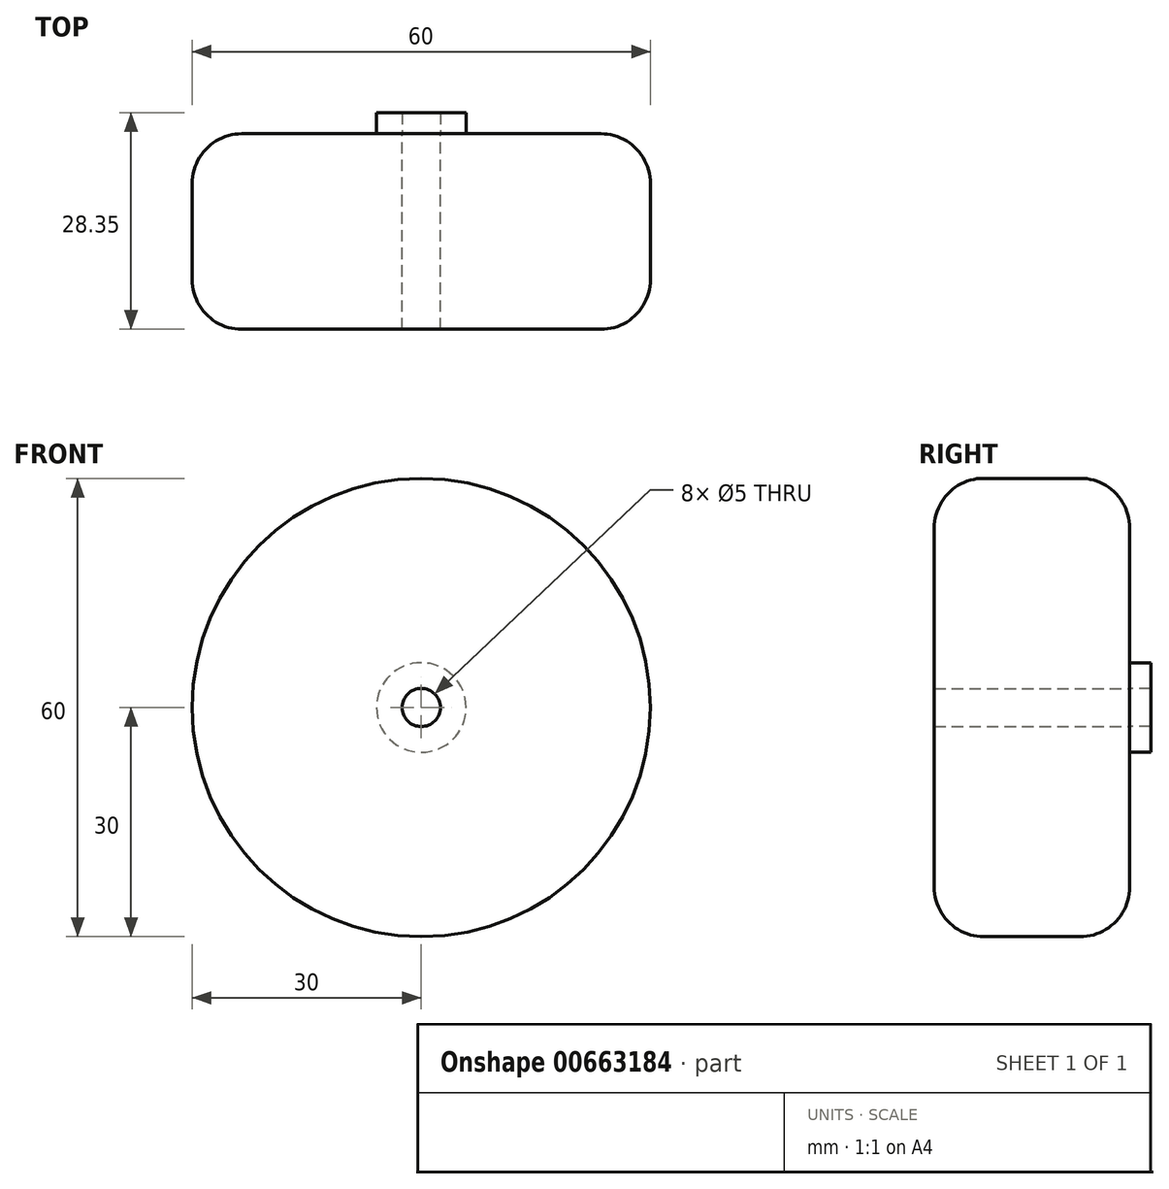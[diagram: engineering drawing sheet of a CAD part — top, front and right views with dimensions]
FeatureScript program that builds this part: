
annotation { "Feature Type Name" : "Feature", "Feature Type Description" : "" }
export const myFeature = defineFeature(function(context is Context, id is Id, definition is map)
    precondition{}
    {
        {
            var Q0;
            Q0=qCreatedBy(makeId("Front.planeOp"),FACE);
            var sketch = newSketch(context, id + "F0", { "sketchPlane" : qUnion([Q0])});
            skCircle(sketch, "E0", {"center": v(0, 0) * mm, "radius": 30 * mm});
            skCircle(sketch, "E1", {"center": v(0, 0) * mm, "radius": 5.86 * mm});
            skCircle(sketch, "E2", {"center": v(0, 0) * mm, "radius": 2.5 * mm});
            skSolve(sketch);
        }
        {
            var Q0;
            Q0=makeQuery(id+"F0.imprint","IMPRINT",FACE,{"disambiguationData":[TD([[makeQuery(id+"F0.imprint","IMPRINT",EDGE,{"derivedFrom":sQuery(id+"F0.wireOp",EDGE,"E0")}),1.0]])]});
            var Q1;
            Q1=makeQuery(id+"F0.imprint","IMPRINT",FACE,{"disambiguationData":[TD([[makeQuery(id+"F0.imprint","IMPRINT",EDGE,{"derivedFrom":sQuery(id+"F0.wireOp",EDGE,"E1")}),1.0]])]});
            extrude(context, id + "F1", {"entities" : qUnion([Q0, Q1]), "depth" : 25.6 * mm, "offsetDistance" : 25 * mm});
        }
        {
            var Q0;
            Q0=makeQuery(id+"F1.opExtrude","CAP_EDGE",EDGE,{"disambiguationData":[OSD([sQuery(id+"F0.wireOp",EDGE,"E0")])],"isStart":false});
            var Q1;
            Q1=makeQuery(id+"F1.opExtrude","CAP_EDGE",EDGE,{"disambiguationData":[OSD([sQuery(id+"F0.wireOp",EDGE,"E0")])],"isStart":true});
            fillet(context, id + "F2", {"entities" : qUnion([Q0, Q1]), "radius" : 6.5 * mm, "tangentPropagation" : true, "allowEdgeOverflow" : false});
        }
        {
            var Q0;
            Q0=makeQuery(id+"F0.imprint","IMPRINT",FACE,{"disambiguationData":[TD([[makeQuery(id+"F0.imprint","IMPRINT",EDGE,{"derivedFrom":sQuery(id+"F0.wireOp",EDGE,"E1")}),1.0]])]});
            extrude(context, id + "F3", {"entities" : qUnion([Q0]), "oppositeDirection" : true, "depth" : 2.75 * mm, "offsetDistance" : 25 * mm});
        }
    });
